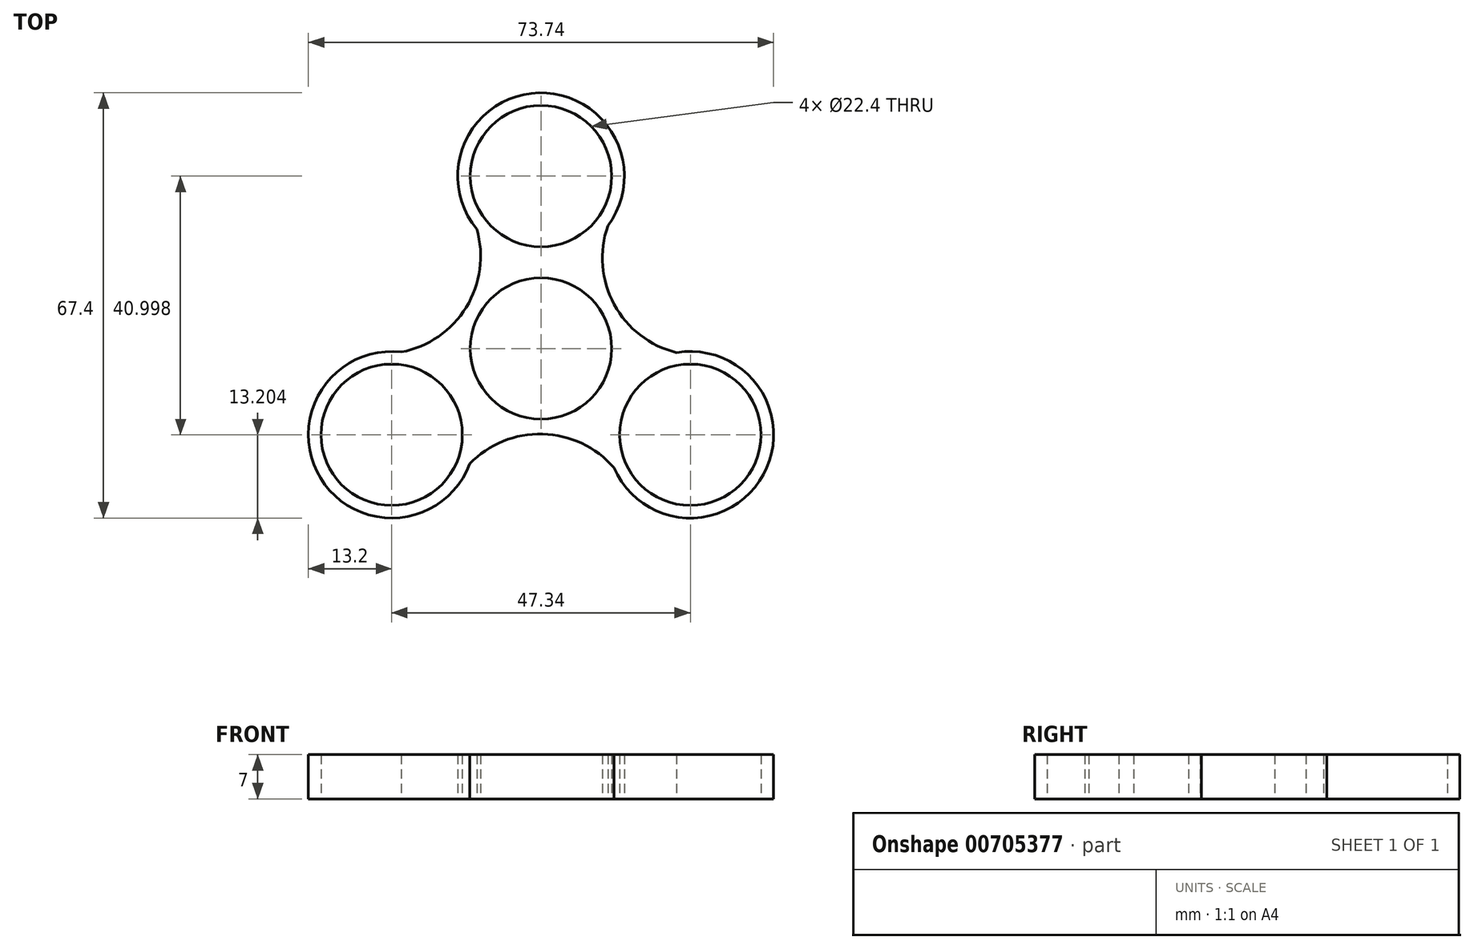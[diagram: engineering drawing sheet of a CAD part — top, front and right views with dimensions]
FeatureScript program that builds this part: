
annotation { "Feature Type Name" : "Feature", "Feature Type Description" : "" }
export const myFeature = defineFeature(function(context is Context, id is Id, definition is map)
    precondition{}
    {
        {
            var Q0;
            Q0=qCreatedBy(makeId("Top.planeOp"),FACE);
            var sketch = newSketch(context, id + "F0", { "sketchPlane" : qUnion([Q0])});
            skCircle(sketch, "E0", {"center": v(0, 0) * mm, "radius": 11.2 * mm});
            skCircle(sketch, "E1", {"center": v(0, 27.33) * mm, "radius": 11.2 * mm});
            skArc(sketch, "E2", {"start": v(10.59, 19.45) * mm, "mid": v(-0.34, 40.53) * mm, "end": v(-10.17, 18.92) * mm});
            skCircle(sketch, "E3.1.0", {"center": v(-23.67, -13.67) * mm, "radius": 11.2 * mm});
            skArc(sketch, "E3.1.1", {"start": v(-22.13, -0.56) * mm, "mid": v(-34.93, -20.55) * mm, "end": v(-11.3, -18.27) * mm});
            skCircle(sketch, "E3.2.0", {"center": v(23.67, -13.67) * mm, "radius": 11.2 * mm});
            skArc(sketch, "E3.2.1", {"start": v(11.55, -18.9) * mm, "mid": v(35.27, -19.97) * mm, "end": v(21.47, -0.65) * mm});
            skArc(sketch, "E4", {"start": v(10.59, 19.45) * mm, "mid": v(11.6, 7) * mm, "end": v(21.47, -0.65) * mm});
            skArc(sketch, "E5.1.0", {"start": v(-22.13, -0.56) * mm, "mid": v(-11.86, 6.54) * mm, "end": v(-10.17, 18.92) * mm});
            skArc(sketch, "E5.2.0", {"start": v(11.55, -18.9) * mm, "mid": v(0.26, -13.54) * mm, "end": v(-11.3, -18.27) * mm});
            skSolve(sketch);
        }
        {
            var Q0;
            Q0=makeQuery(id+"F0.imprint","IMPRINT",FACE,{"disambiguationData":[TD([[makeQuery(id+"F0.imprint","IMPRINT",EDGE,{"derivedFrom":sQuery(id+"F0.wireOp",EDGE,"E0")}),-1.0]])]});
            extrude(context, id + "F1", {"entities" : qUnion([Q0]), "depth" : 7 * mm, "offsetDistance" : 25 * mm});
        }
    });
